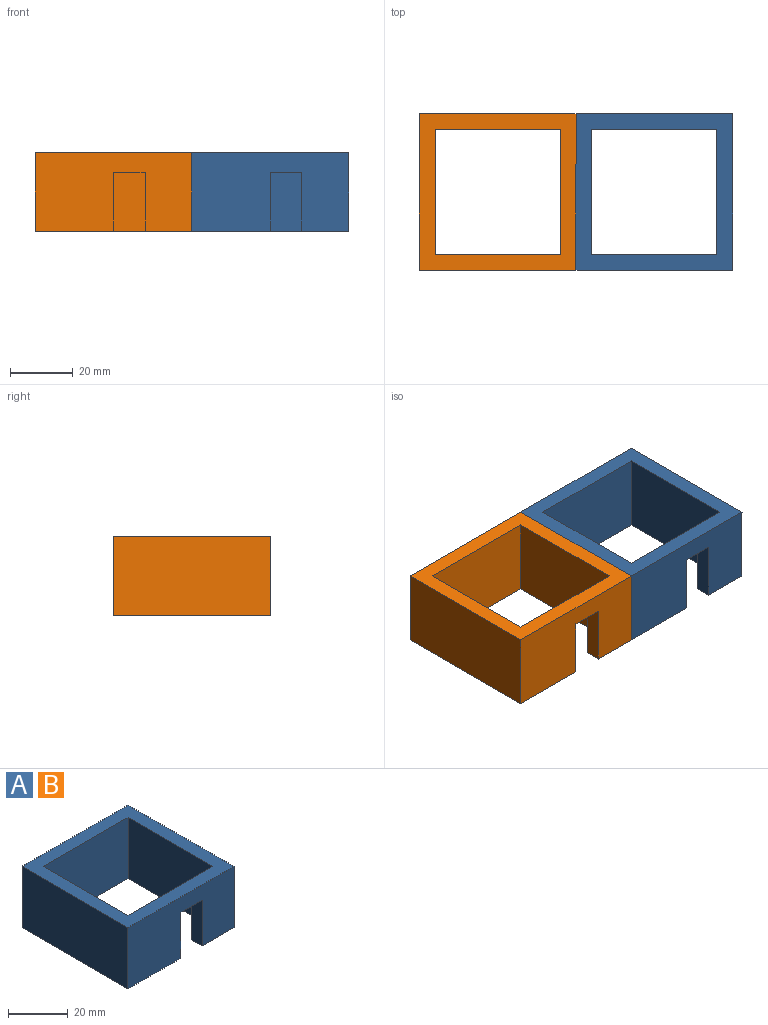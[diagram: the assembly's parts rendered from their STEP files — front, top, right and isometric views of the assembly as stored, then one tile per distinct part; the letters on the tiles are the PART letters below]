
ASSEMBLY  parts=2 mates=1
PART A: 13 faces, bbox 50x50x25 mm
  f0: plane 40x25mm, normal (0,1,0), area 812.4mm2, adj f2,f7,f8,f9,f10,f11,f12
  f1: plane 40x25mm, normal (0,-1,0), area 1000mm2, adj f2,f7,f8,f9
  f2: plane 40x25mm, normal (-1,0,0), area 1000mm2, adj f0,f1,f8,f9
  f3: plane 50x25mm, normal (-1,0,0), area 1250mm2, adj f4,f6,f8,f9
  f4: plane 50x25mm, normal (0,-1,0), area 1062.4mm2, adj f3,f5,f8,f9,f10,f11,f12
  f5: plane 50x25mm, normal (1,0,0), area 1250mm2, adj f4,f6,f8,f9
  f6: plane 50x25mm, normal (0,1,0), area 1250mm2, adj f3,f5,f8,f9
  f7: plane 40x25mm, normal (1,0,0), area 1000mm2, adj f0,f1,f8,f9
  f8: plane 50x50mm, normal (0,0,1), area 900mm2, adj f0,f1,f2,f3,f4,f5,f6,f7
  f9: plane 50x50mm, normal (0,0,-1), area 850mm2, adj f0,f1,f2,f3,f4,f5,f6,f7
  f10: plane 10x5mm, normal (0,0,-1), area 50mm2, adj f0,f4,f11,f12
  f11: plane 18.76x5mm, normal (1,0,0), area 93.8mm2, adj f0,f4,f9,f10
  f12: plane 18.76x5mm, normal (-1,0,0), area 93.8mm2, adj f0,f4,f9,f10
PART B: same geometry as A
PLACE A t=(6.53,-21.2,13.13)mm
PLACE B t=(-43.47,-21.2,13.13)mm
MATE fastened A.f3 <-> B.f5  axis (1,0,0) through (6.53,3.8,25.63)mm
